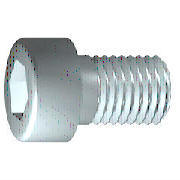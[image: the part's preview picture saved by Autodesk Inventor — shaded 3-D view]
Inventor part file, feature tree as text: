
AUTODESK INVENTOR PART (.ipt)
format: ipt  version: 2015 (Build 190159000, 159)  size: 190,976 bytes
history: native  units: mm (DEFAULTED — no unit token found)
features: sketch x2, extrude x1, plane x1, fillet x1
ambient origin geometry x7: Origin, YZ Plane, XY Plane, X Axis, Y Axis, Z Axis, Center Point
bodies: Solid1 (feature_tree), Body (feature_tree)
feature tree (5):
  extrude  "Slot"  Depth=5.0mm
  plane  "Work Plane1"
  fillet  "Fillet2"  Radius=5.0mm
  sketch  "Sketch1"  dims[d1=22.0mm d2=0.49086mm d3=5.0mm]
  sketch  "Sketch2"  dims[d4=2.5mm d5=60.0deg d6=5.0mm d7=5.0mm d8=4.618802mm d9=8.5mm d10=90.0deg d11=10.0mm d12=0.0mm d13=22.0mm d14=0.0mm d15=0.49076mm d16=0.49076mm d17=0.5mm d19=0.0mm d26=35.0mm d27=45.0deg d28=0.0mm d29=0.0mm d30=0.1mm]
